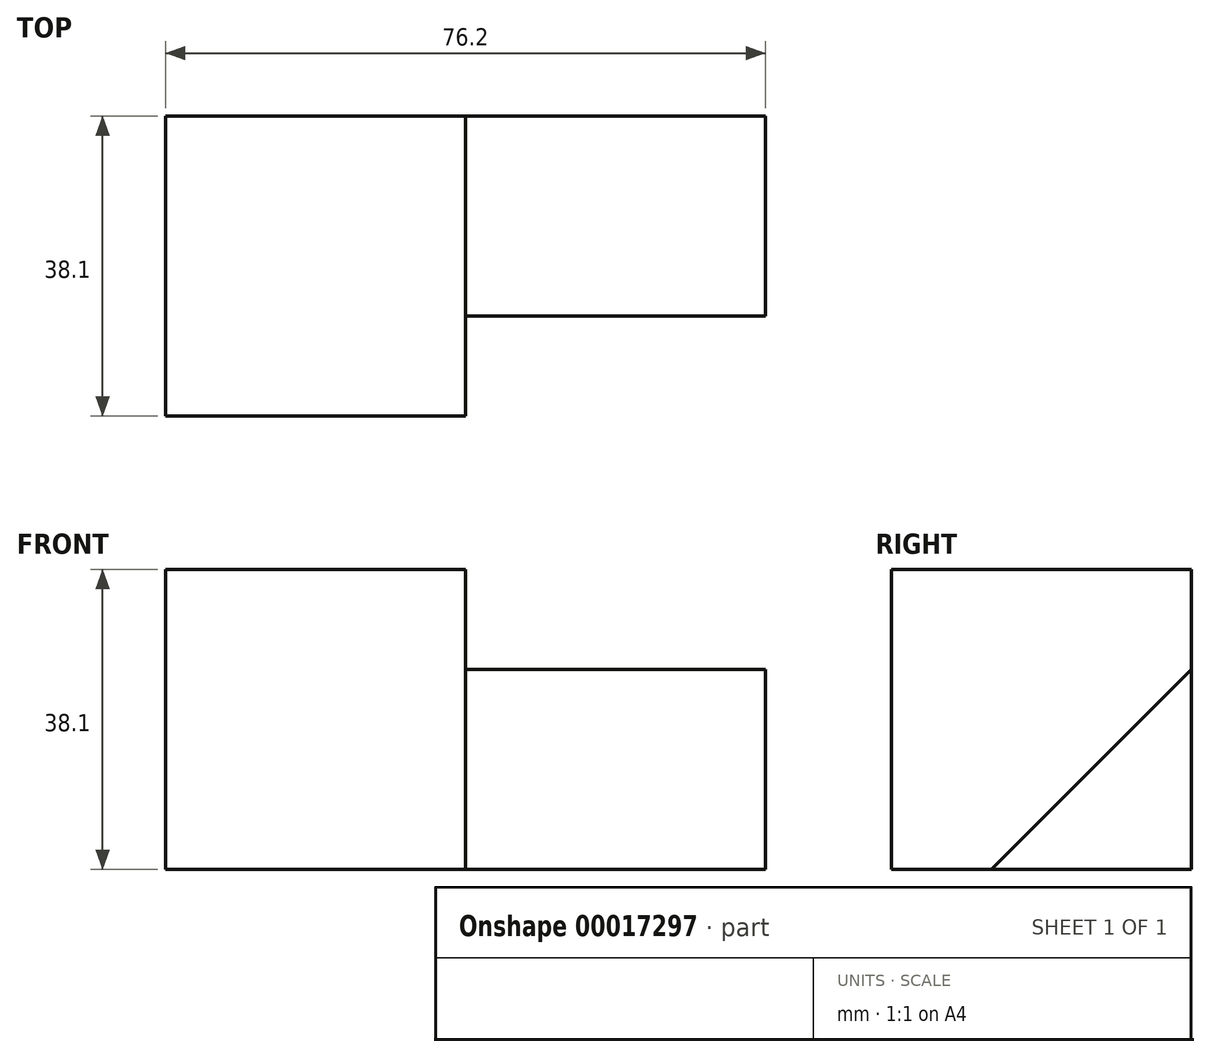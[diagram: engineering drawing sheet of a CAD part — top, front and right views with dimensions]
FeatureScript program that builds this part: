
annotation { "Feature Type Name" : "Feature", "Feature Type Description" : "" }
export const myFeature = defineFeature(function(context is Context, id is Id, definition is map)
    precondition{}
    {
        {
            var Q0;
            Q0=qCreatedBy(makeId("Front.planeOp"),FACE);
            var sketch = newSketch(context, id + "F0", { "sketchPlane" : qUnion([Q0])});
            skLineSegment(sketch, "E0", {"start": v(-15.48, 8.95) * mm, "end": v(-15.48, -29.15) * mm});
            skLineSegment(sketch, "E1", {"start": v(-15.48, -29.15) * mm, "end": v(22.62, -29.15) * mm});
            skLineSegment(sketch, "E2", {"start": v(22.62, -29.15) * mm, "end": v(22.62, 8.95) * mm});
            skLineSegment(sketch, "E3", {"start": v(-15.48, 8.95) * mm, "end": v(22.62, 8.95) * mm});
            skSolve(sketch);
        }
        {
            var Q0;
            Q0 = qSketchRegion(id + "F0", true);
            extrude(context, id + "F1", {"entities" : qUnion([Q0]), "depth" : 38.1 * mm});
        }
        {
            var Q0;
            Q0=makeQuery(id+"F1.opExtrude","SWEPT_FACE",FACE,{"disambiguationData":[OSD([sQuery(id+"F0.wireOp",EDGE,"E2")])]});
            var sketch = newSketch(context, id + "F2", { "sketchPlane" : qUnion([Q0])});
            skLineSegment(sketch, "E4", {"start": v(0, -29.15) * mm, "end": v(-25.4, -29.15) * mm});
            skLineSegment(sketch, "E5", {"start": v(-25.4, -29.15) * mm, "end": v(0, -3.75) * mm});
            skLineSegment(sketch, "E6", {"start": v(0, -3.75) * mm, "end": v(0, -29.15) * mm});
            skSolve(sketch);
        }
        {
            var Q0;
            Q0 = qSketchRegion(id + "F2", true);
            extrude(context, id + "F3", {"entities" : qUnion([Q0]), "operationType" : NewBodyOperationType.ADD, "depth" : 38.1 * mm});
        }
    });
